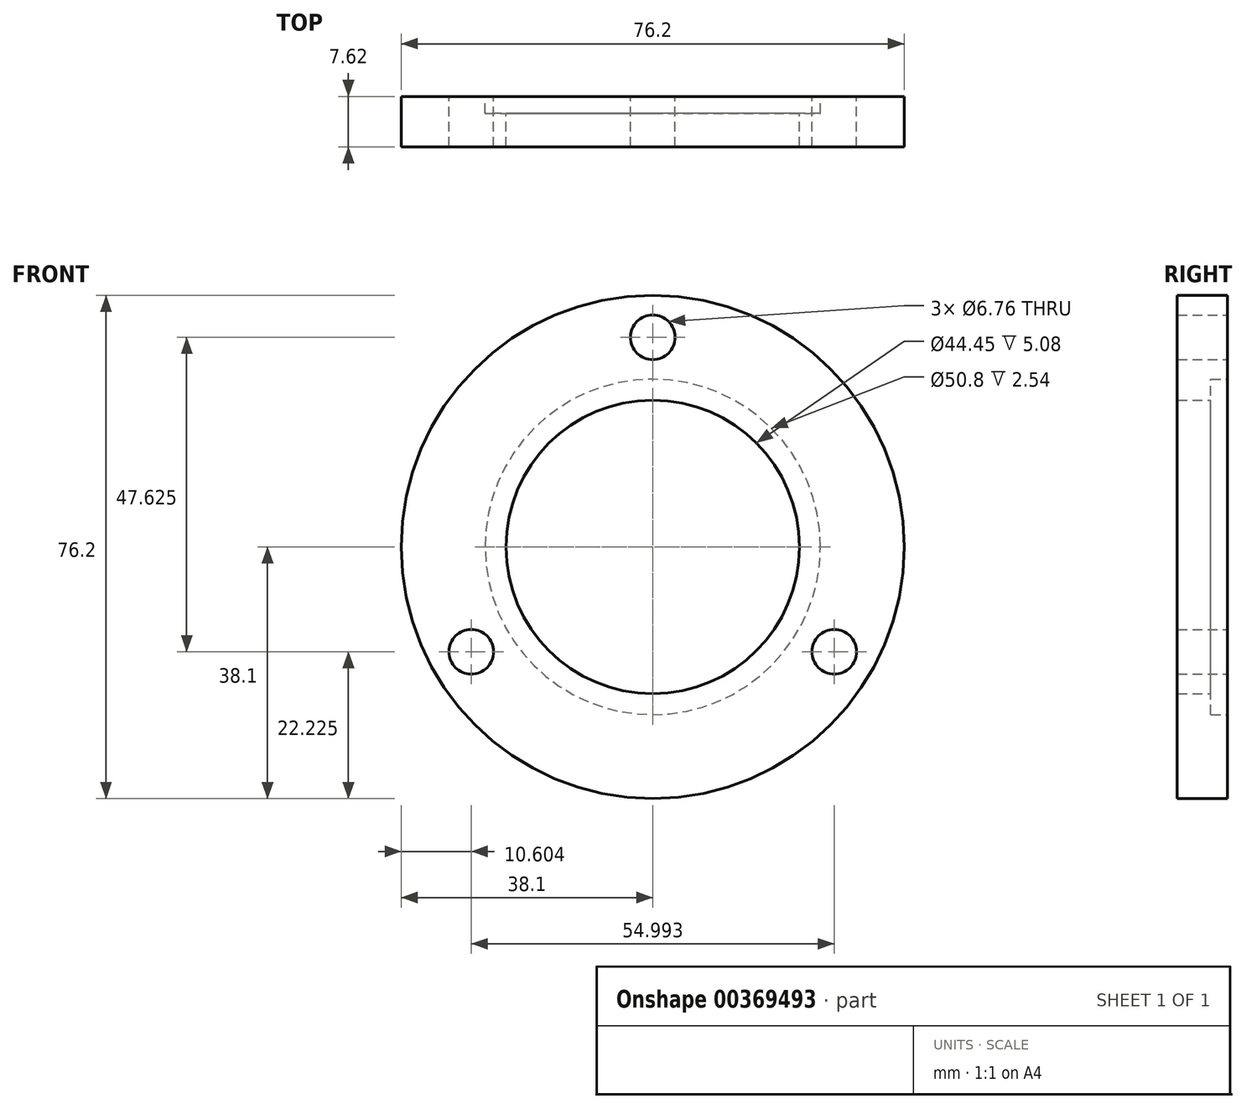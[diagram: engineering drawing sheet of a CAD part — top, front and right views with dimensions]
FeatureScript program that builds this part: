
annotation { "Feature Type Name" : "Feature", "Feature Type Description" : "" }
export const myFeature = defineFeature(function(context is Context, id is Id, definition is map)
    precondition{}
    {
        {
            var Q0;
            Q0=qCreatedBy(makeId("Front.planeOp"),FACE);
            var sketch = newSketch(context, id + "F0", { "sketchPlane" : qUnion([Q0])});
            skCircle(sketch, "E0", {"center": v(0, 0) * mm, "radius": 38.1 * mm});
            skCircle(sketch, "E1", {"center": v(0, 0) * mm, "radius": 22.23 * mm});
            skCircle(sketch, "E2", {"center": v(0, 0) * mm, "radius": 25.4 * mm});
            skCircle(sketch, "E3", {"center": v(0, 0) * mm, "radius": 31.75 * mm});
            skCircle(sketch, "E4", {"center": v(0, 31.75) * mm, "radius": 2.19 * mm});
            skCircle(sketch, "E5.1.0", {"center": v(-27.5, -15.87) * mm, "radius": 2.19 * mm});
            skCircle(sketch, "E5.2.0", {"center": v(27.5, -15.88) * mm, "radius": 2.19 * mm});
            skSolve(sketch);
        }
        {
            var Q0;
            Q0 = qSketchRegion(id + "F0", true);
            var Q1;
            Q1=makeQuery(id+"F0.imprint","IMPRINT",FACE,{"disambiguationData":[TD([[makeQuery(id+"F0.imprint","IMPRINT",EDGE,{"derivedFrom":sQuery(id+"F0.wireOp",EDGE,"E2")}),-1.0]])]});
            var Q2;
            Q2=makeQuery(id+"F0.imprint","IMPRINT",FACE,{"disambiguationData":[TD([[makeQuery(id+"F0.imprint","IMPRINT",EDGE,{"derivedFrom":sQuery(id+"F0.wireOp",EDGE,"E1")}),-1.0]])]});
            var Q3;
            {var subQ0=sQuery(id+"F0.wireOp",EDGE,"E4");var subQ1=sQuery(id+"F0.wireOp",EDGE,"E3");var subQ2=makeQuery(id+"F0.imprint","INTERSECT",VERTEX,{"disambiguationData":[OD(0.0)],"derivedFrom":[subQ1,subQ0]});Q3=makeQuery(id+"F0.imprint","IMPRINT",FACE,{"disambiguationData":[TD([[makeQuery(id+"F0.imprint","IMPRINT",EDGE,{"disambiguationData":[TD([[subQ2,1.0]])],"derivedFrom":subQ1}),-1.0]])]});}
            var Q4;
            {var subQ0=sQuery(id+"F0.wireOp",EDGE,"E4");var subQ1=sQuery(id+"F0.wireOp",EDGE,"E3");var subQ2=makeQuery(id+"F0.imprint","INTERSECT",VERTEX,{"disambiguationData":[OD(0.0)],"derivedFrom":[subQ1,subQ0]});Q4=makeQuery(id+"F0.imprint","IMPRINT",FACE,{"disambiguationData":[TD([[makeQuery(id+"F0.imprint","IMPRINT",EDGE,{"disambiguationData":[TD([[subQ2,1.0]])],"derivedFrom":subQ1}),1.0]])]});}
            var Q5;
            {var subQ0=sQuery(id+"F0.wireOp",EDGE,"E5.1.0");var subQ1=sQuery(id+"F0.wireOp",EDGE,"E3");var subQ2=makeQuery(id+"F0.imprint","INTERSECT",VERTEX,{"disambiguationData":[OD(0.0)],"derivedFrom":[subQ1,subQ0]});Q5=makeQuery(id+"F0.imprint","IMPRINT",FACE,{"disambiguationData":[TD([[makeQuery(id+"F0.imprint","IMPRINT",EDGE,{"disambiguationData":[TD([[subQ2,-1.0]])],"derivedFrom":subQ1}),-1.0]])]});}
            var Q6;
            {var subQ0=sQuery(id+"F0.wireOp",EDGE,"E5.1.0");var subQ1=sQuery(id+"F0.wireOp",EDGE,"E3");var subQ2=makeQuery(id+"F0.imprint","INTERSECT",VERTEX,{"disambiguationData":[OD(0.0)],"derivedFrom":[subQ1,subQ0]});Q6=makeQuery(id+"F0.imprint","IMPRINT",FACE,{"disambiguationData":[TD([[makeQuery(id+"F0.imprint","IMPRINT",EDGE,{"disambiguationData":[TD([[subQ2,-1.0]])],"derivedFrom":subQ1}),1.0]])]});}
            var Q7;
            {var subQ0=sQuery(id+"F0.wireOp",EDGE,"E5.2.0");var subQ1=sQuery(id+"F0.wireOp",EDGE,"E3");var subQ2=makeQuery(id+"F0.imprint","INTERSECT",VERTEX,{"disambiguationData":[OD(0.0)],"derivedFrom":[subQ1,subQ0]});Q7=makeQuery(id+"F0.imprint","IMPRINT",FACE,{"disambiguationData":[TD([[makeQuery(id+"F0.imprint","IMPRINT",EDGE,{"disambiguationData":[TD([[subQ2,-1.0]])],"derivedFrom":subQ1}),-1.0]])]});}
            var Q8;
            {var subQ0=sQuery(id+"F0.wireOp",EDGE,"E5.2.0");var subQ1=sQuery(id+"F0.wireOp",EDGE,"E3");var subQ2=makeQuery(id+"F0.imprint","INTERSECT",VERTEX,{"disambiguationData":[OD(0.0)],"derivedFrom":[subQ1,subQ0]});Q8=makeQuery(id+"F0.imprint","IMPRINT",FACE,{"disambiguationData":[TD([[makeQuery(id+"F0.imprint","IMPRINT",EDGE,{"disambiguationData":[TD([[subQ2,-1.0]])],"derivedFrom":subQ1}),1.0]])]});}
            extrude(context, id + "F1", {"entities" : qUnion([Q0, Q1, Q2, Q3, Q4, Q5, Q6, Q7, Q8]), "depth" : 7.62 * mm});
        }
        {
            var Q0;
            Q0=makeQuery(id+"F0.imprint","IMPRINT",FACE,{"disambiguationData":[TD([[makeQuery(id+"F0.imprint","IMPRINT",EDGE,{"derivedFrom":sQuery(id+"F0.wireOp",EDGE,"E1")}),-1.0]])]});
            extrude(context, id + "F2", {"entities" : qUnion([Q0]), "operationType" : NewBodyOperationType.REMOVE, "depth" : 2.54 * mm});
        }
        {
            var Q0;
            Q0=sQuery(id+"F0.wireOp",VERTEX,"E5.2.0.center");
            var Q1;
            Q1=sQuery(id+"F0.wireOp",VERTEX,"E5.1.0.center");
            var Q2;
            Q2=sQuery(id+"F0.wireOp",VERTEX,"E4.center");
            var Q3;
            Q3=makeQuery(id+"F1.opExtrude","SWEPT_BODY",BODY,{"disambiguationData":[OSD([sQuery(id+"F0.wireOp",EDGE,"E0"),sQuery(id+"F0.wireOp",EDGE,"E1")])]});
            hole(context, id + "F3", {"style" : HoleStyle.SIMPLE, "endStyle" : HoleEndStyle.THROUGH, "oppositeDirection" : true, "standardTappedOrClearance" : lookupTablePath({ "standard" : "ANSI", "fit" : "Normal (ASME)", "size" : "1/4", "type" : "Clearance" }), "standardBlindInLast" : lookupTablePath({ "fit" : "Free", "standard" : "ANSI", "size" : "1/4", "type" : "Clearance" }), "holeDiameter" : 6.76 * mm, "isTappedThrough" : true, "tappedDepth" : 6.86 * mm, "tapClearance" : 3, "locations" : qUnion([Q0, Q1, Q2]), "scope" : qUnion([Q3])});
        }
    });
